# Revit family: Electronics_Community-Point-Source_Biamp_Loudspeaker_V2_1596
name_source: partatom
category: Communication Devices
units: mm (PartAtom-declared; Revit-internal decimal feet)

## family parameters
Cut with Voids When Loaded = No
Host = Face
Maintain Annotation Orientation = No
OmniClass Number = 23.85.10.11.14.14.14
Part Type = Normal
Room Calculation Point = No
Round Connector Dimension = Use Diameter
Shared = No

## types (2) — shared parameters
Connector Description = NL4, Terminal strip; 200W continuous, 500W program 40 volts RMS, 80 volts momentary peak
Crossover Frequency = 1.3 kHz
Default Elevation = 4' - 0"
Depth = 1' - 4"
Description = V2-1596 15-Inch, Two-Way, Full-Range Loudspeaker System (90° x 60°)
Driver Protection = DYNA-TECH protection circuitry
Drivers = LF 1 x 15-inch cone, HF 1 x 1-inch
Enclosure = Trapezoidal (22.5° included angle) 18mm, 11-ply cross-laminated birch
Frequency Response = 80 Hz to 16 kHz (±3 dB)
Height = 2' - 3"
Input Connection = NL4-compatible locking connector with terminal strip in parallel
Loudspeaker Type = Two-way, full-range, trapezoidal, vented bass
Manufacturer = Biamp
Maximum Output = 121 dB SPL / 127 dB SPL (peak)
Minimum Impedance = 6.4 ohms @ 140 Hz
Mounting/Rigging Provisions = 13 x M10 threaded rigging fittings, 4 x M8 threaded fittings for third-party suspension products
Nominal Impedance = 8 ohms
Nominal –6dB Beamwidth = 90° H x 60° V (in vertical position)
Operating Range = 60 Hz to 18 kHz (-10 dB)
Optional Accessories = VB-Y15 U-shaped yoke bracket, VB-VY15 vertical yoke bracket, CMKIT ceiling mount kit, VB-TILT tilting bracket, VB-VST versatilt bracket, VFKIT vertical flying kit, M10EYBLTKIT 10mm eyebolt kit, STKIT seat track kit
Product Documentation Link = https://downloads.biamp.com
Product Page URL = https://www.biamp.com
Product data url = https://www.bimobject.com
Recommended Signal Processing = 60 Hz, 24 dB/octave Butterworth high pass filter
Sensitivity (1W/1m) = 98 dB  (100 Hz to 12.5 kHz) free space
URL = https://www.biamp.com
Weight = 47.80 lbf
Width = 1' - 6 1/2"

## per-type parameters (varying)
| type | Grill Material | Housing Material |
| V2-1596 B | Biamp - Plastic - Black(Grid) | Biamp - Plastic - Black |
| V2-1596 W | Biamp - Plastic - White(Grid) | Biamp - Plastic - White |

note: column(s) folded — value = type name in every type: Model

## geometry (parser evidence)
native form markers: Sweep x2
no freeform markers — native parametric forms only
